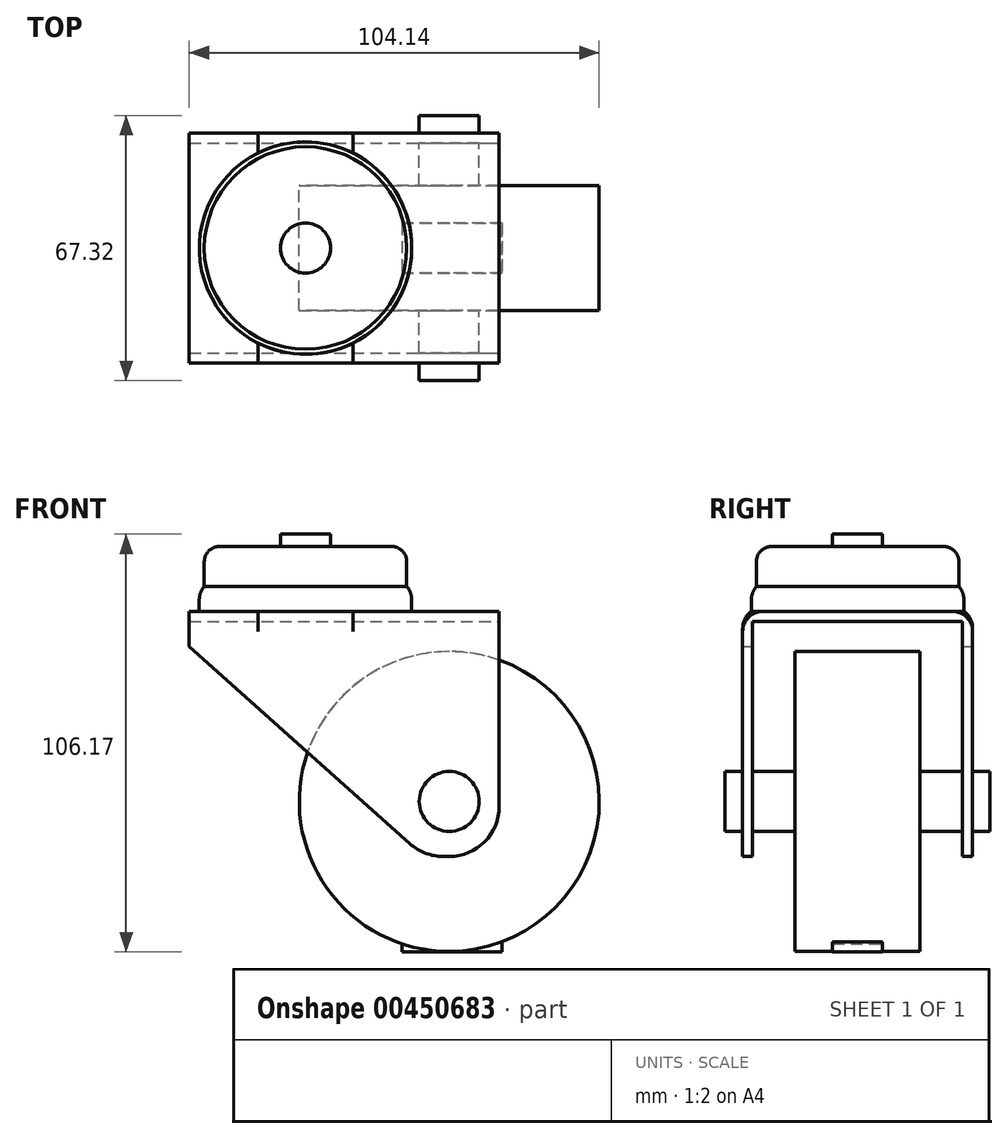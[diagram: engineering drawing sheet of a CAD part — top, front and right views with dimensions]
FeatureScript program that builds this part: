
annotation { "Feature Type Name" : "Feature", "Feature Type Description" : "" }
export const myFeature = defineFeature(function(context is Context, id is Id, definition is map)
    precondition{}
    {
        {
            var Q0;
            Q0=qCreatedBy(makeId("Front.planeOp"),FACE);
            var sketch = newSketch(context, id + "F0", { "sketchPlane" : qUnion([Q0])});
            skLineSegment(sketch, "E0.bottom", {"start": v(-39.37, 31.12) * mm, "end": v(39.37, 31.12) * mm});
            skLineSegment(sketch, "E0.top", {"start": v(25.17, -31.11) * mm, "end": v(26.67, -31.11) * mm});
            skLineSegment(sketch, "E0.left", {"start": v(-39.37, 31.12) * mm, "end": v(-39.37, 22.23) * mm});
            skLineSegment(sketch, "E0.right", {"start": v(39.37, 31.12) * mm, "end": v(39.37, -18.42) * mm});
            skLineSegment(sketch, "E1", {"start": v(-39.37, 22.23) * mm, "end": v(16.7, -27.88) * mm});
            skLineSegment(sketch, "E2", {"start": v(-39.37, 31.11) * mm, "end": v(39.37, -31.11) * mm, "construction": true});
            skCircle(sketch, "E3", {"center": v(26.67, -17.14) * mm, "radius": 7.62 * mm});
            skPoint(sketch, "E4.visualSharp", {"position": v(39.37, -31.11) * mm});
            skArc(sketch, "E4.filletArc", {"start": v(26.67, -31.12) * mm, "mid": v(35.65, -27.4) * mm, "end": v(39.37, -18.42) * mm});
            skPoint(sketch, "E5.visualSharp", {"position": v(20.32, -31.12) * mm});
            skArc(sketch, "E5.filletArc", {"start": v(16.7, -27.88) * mm, "mid": v(20.64, -30.28) * mm, "end": v(25.17, -31.12) * mm});
            skSolve(sketch);
        }
        {
            var Q0;
            Q0 = qSketchRegion(id + "F0", true);
            extrude(context, id + "F1", {"entities" : qUnion([Q0]), "depth" : 58.42 * mm, "symmetric" : true});
        }
        {
            var Q0;
            Q0=makeQuery(id+"F1.opExtrude","SWEPT_FACE",FACE,{"disambiguationData":[OSD([sQuery(id+"F0.wireOp",EDGE,"E0.right")])]});
            var sketch = newSketch(context, id + "F2", { "sketchPlane" : qUnion([Q0])});
            skLineSegment(sketch, "E6.bottom", {"start": v(-26.67, 28.58) * mm, "end": v(26.67, 28.58) * mm});
            skLineSegment(sketch, "E6.top", {"start": v(-26.67, -47.62) * mm, "end": v(26.67, -47.62) * mm});
            skLineSegment(sketch, "E6.left", {"start": v(-26.67, 28.58) * mm, "end": v(-26.67, -47.62) * mm});
            skLineSegment(sketch, "E6.right", {"start": v(26.67, 28.58) * mm, "end": v(26.67, -47.62) * mm});
            skSolve(sketch);
        }
        {
            var Q0;
            Q0 = qSketchRegion(id + "F2", true);
            extrude(context, id + "F3", {"entities" : qUnion([Q0]), "operationType" : NewBodyOperationType.REMOVE, "endBound" : BoundingType.THROUGH_ALL, "oppositeDirection" : true, "depth" : 25.4 * mm});
        }
        {
            var Q0;
            Q0=qCreatedBy(makeId("Front.planeOp"),FACE);
            var sketch = newSketch(context, id + "F4", { "sketchPlane" : qUnion([Q0])});
            skCircle(sketch, "E7.0", {"center": v(26.67, -17.14) * mm, "radius": 7.62 * mm});
            skSolve(sketch);
        }
        {
            var Q0;
            Q0 = qSketchRegion(id + "F4", true);
            extrude(context, id + "F5", {"entities" : qUnion([Q0]), "operationType" : NewBodyOperationType.ADD, "depth" : 67.3 * mm, "symmetric" : true});
        }
        {
            var Q0;
            Q0=qCreatedBy(makeId("Front.planeOp"),FACE);
            var sketch = newSketch(context, id + "F6", { "sketchPlane" : qUnion([Q0])});
            skCircle(sketch, "E8", {"center": v(26.67, -17.14) * mm, "radius": 38.1 * mm});
            skSolve(sketch);
        }
        {
            var Q0;
            Q0 = qSketchRegion(id + "F6", true);
            extrude(context, id + "F7", {"entities" : qUnion([Q0]), "operationType" : NewBodyOperationType.ADD, "depth" : 31.75 * mm, "symmetric" : true});
        }
        {
            var Q0;
            Q0=makeQuery(id+"F1.opExtrude","SWEPT_FACE",FACE,{"disambiguationData":[OSD([sQuery(id+"F0.wireOp",EDGE,"E0.bottom")])]});
            var sketch = newSketch(context, id + "F8", { "sketchPlane" : qUnion([Q0])});
            skCircle(sketch, "E9", {"center": v(-9.84, 0) * mm, "radius": 26.99 * mm});
            skSolve(sketch);
        }
        {
            var Q0;
            Q0 = qSketchRegion(id + "F8", true);
            extrude(context, id + "F9", {"entities" : qUnion([Q0]), "operationType" : NewBodyOperationType.ADD, "depth" : 6.35 * mm});
        }
        {
            var Q0;
            Q0=makeQuery(id+"F9.opExtrude","CAP_FACE",FACE,{"disambiguationData":[OSD([sQuery(id+"F8.wireOp",EDGE,"E9")])],"isStart":false});
            var sketch = newSketch(context, id + "F10", { "sketchPlane" : qUnion([Q0])});
            skCircle(sketch, "E10.0", {"center": v(-9.84, 0) * mm, "radius": 25.72 * mm});
            skSolve(sketch);
        }
        {
            var Q0;
            Q0 = qSketchRegion(id + "F10", true);
            extrude(context, id + "F11", {"entities" : qUnion([Q0]), "operationType" : NewBodyOperationType.ADD, "depth" : 10.16 * mm});
        }
        {
            var Q0;
            Q0=makeQuery(id+"F9.opExtrude","CAP_EDGE",EDGE,{"disambiguationData":[OSD([sQuery(id+"F8.wireOp",EDGE,"E9")])],"isStart":false});
            fillet(context, id + "F12", {"entities" : qUnion([Q0]), "radius" : 5.08 * mm, "tangentPropagation" : true, "allowEdgeOverflow" : false});
        }
        {
            var Q0;
            Q0=makeQuery(id+"F1.opExtrude","CAP_EDGE",EDGE,{"disambiguationData":[OSD([sQuery(id+"F0.wireOp",EDGE,"E0.bottom")])],"isStart":false});
            var Q1;
            Q1=makeQuery(id+"F1.opExtrude","CAP_EDGE",EDGE,{"disambiguationData":[OSD([sQuery(id+"F0.wireOp",EDGE,"E0.bottom")])],"isStart":true});
            fillet(context, id + "F13", {"entities" : qUnion([Q0, Q1]), "radius" : 5.08 * mm, "tangentPropagation" : true, "allowEdgeOverflow" : false});
        }
        {
            var Q0;
            Q0=makeQuery(id+"F11.opExtrude","CAP_EDGE",EDGE,{"disambiguationData":[OSD([sQuery(id+"F10.wireOp",EDGE,"E10.0")])],"isStart":false});
            fillet(context, id + "F14", {"entities" : qUnion([Q0]), "radius" : 3.8 * mm, "tangentPropagation" : true, "allowEdgeOverflow" : false});
        }
        {
            var Q0;
            Q0=makeQuery(id+"F11.opExtrude","CAP_FACE",FACE,{"disambiguationData":[OSD([sQuery(id+"F10.wireOp",EDGE,"E10.0")])],"isStart":false});
            var sketch = newSketch(context, id + "F15", { "sketchPlane" : qUnion([Q0])});
            skCircle(sketch, "E11", {"center": v(-9.84, 0) * mm, "radius": 6.35 * mm});
            skSolve(sketch);
        }
        {
            var Q0;
            Q0 = qSketchRegion(id + "F15", true);
            extrude(context, id + "F16", {"entities" : qUnion([Q0]), "operationType" : NewBodyOperationType.ADD, "depth" : 3.17 * mm});
        }
        {
            var Q0;
            Q0=qCreatedBy(makeId("Top.planeOp"),FACE);
            cPlane(context, id + "F17", {"entities" : qUnion([Q0]), "cplaneType" : CPlaneType.OFFSET, "offset" : 55.37 * mm, "oppositeDirection" : true, "width" : 152.4 * mm, "height" : 152.4 * mm});
        }
        {
            var Q0;
            Q0=qCreatedBy(id+"F17.planeOp",FACE);
            var sketch = newSketch(context, id + "F18", { "sketchPlane" : qUnion([Q0])});
            skLineSegment(sketch, "E12.bottom", {"start": v(14.64, 6.35) * mm, "end": v(40.04, 6.35) * mm});
            skLineSegment(sketch, "E12.top", {"start": v(14.64, -6.35) * mm, "end": v(40.04, -6.35) * mm});
            skLineSegment(sketch, "E12.left", {"start": v(14.64, 6.35) * mm, "end": v(14.64, -6.35) * mm});
            skLineSegment(sketch, "E12.right", {"start": v(40.04, 6.35) * mm, "end": v(40.04, -6.35) * mm});
            skLineSegment(sketch, "E13", {"start": v(27.34, -6.35) * mm, "end": v(27.34, -15.87) * mm, "construction": true});
            skLineSegment(sketch, "E14", {"start": v(27.34, 6.35) * mm, "end": v(27.34, 15.88) * mm, "construction": true});
            skSolve(sketch);
        }
        {
            var Q0;
            Q0 = qSketchRegion(id + "F18", true);
            extrude(context, id + "F19", {"entities" : qUnion([Q0]), "operationType" : NewBodyOperationType.ADD, "depth" : 2.54 * mm});
        }
    });
